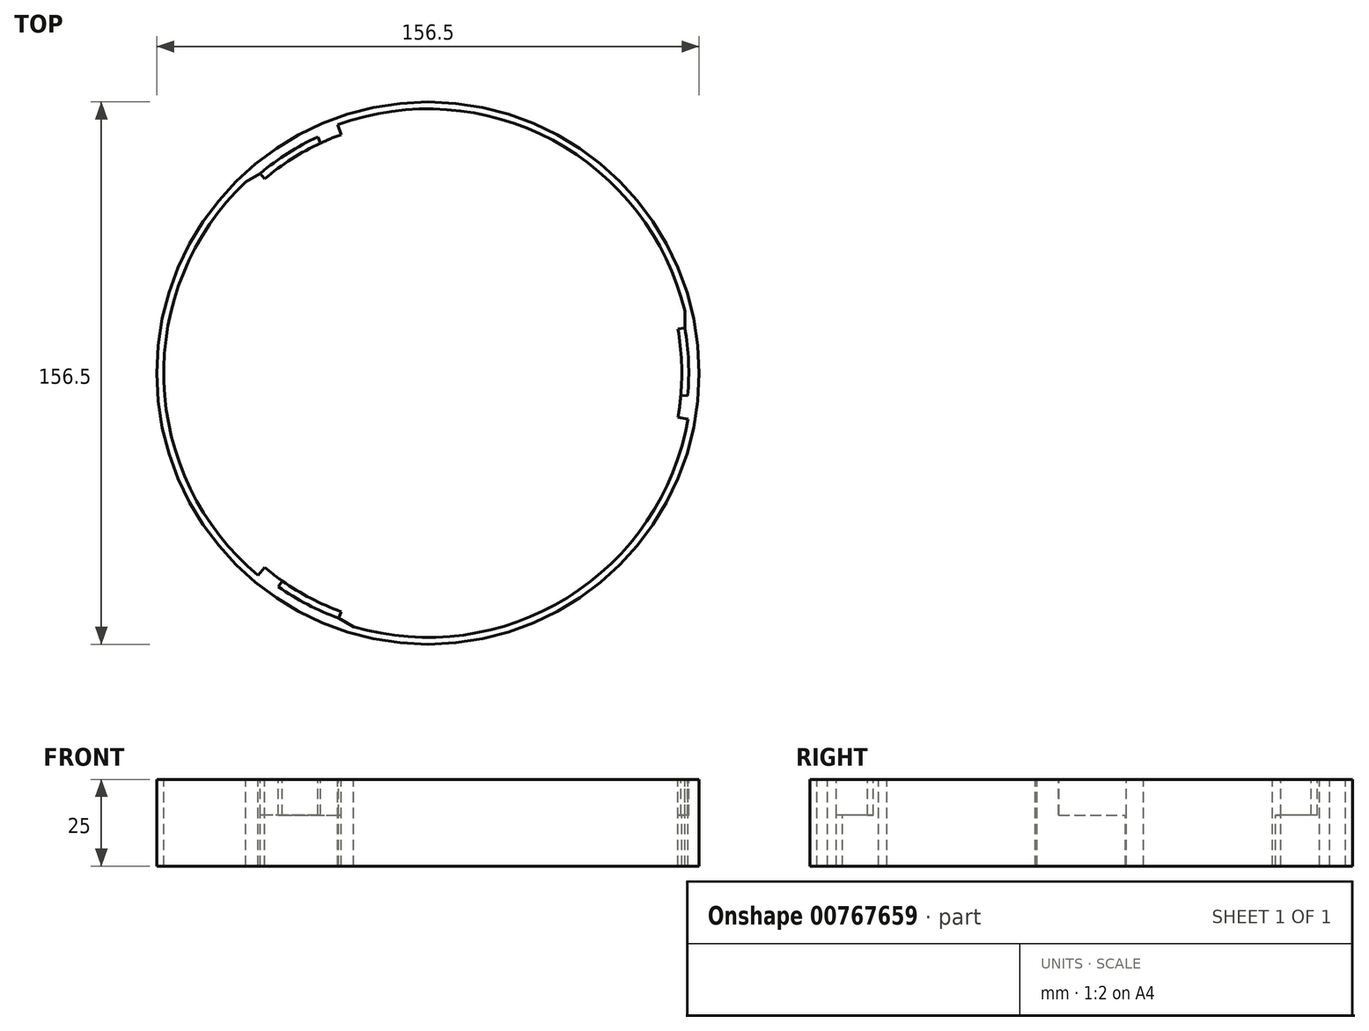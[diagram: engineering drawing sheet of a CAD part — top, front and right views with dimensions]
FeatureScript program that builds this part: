
annotation { "Feature Type Name" : "Feature", "Feature Type Description" : "" }
export const myFeature = defineFeature(function(context is Context, id is Id, definition is map)
    precondition{}
    {
        {
            var Q0;
            Q0=qCreatedBy(makeId("Top.planeOp"),FACE);
            var sketch = newSketch(context, id + "F0", { "sketchPlane" : qUnion([Q0])});
            skArc(sketch, "E0", {"start": v(-31.8, 68.2) * mm, "mid": v(-40.43, 63.47) * mm, "end": v(-48.37, 57.64) * mm});
            skCircle(sketch, "E1", {"center": v(0, 0) * mm, "radius": 78.25 * mm});
            skArc(sketch, "E2", {"start": v(-25.05, 68.83) * mm, "mid": v(-36.63, 63.44) * mm, "end": v(-47.08, 56.11) * mm});
            skLineSegment(sketch, "E3", {"start": v(-47.08, 56.11) * mm, "end": v(-48.37, 57.64) * mm});
            skLineSegment(sketch, "E4", {"start": v(-48.37, 57.64) * mm, "end": v(-52.6, 55.2) * mm});
            skArc(sketch, "E5.trimOffspring", {"start": v(-52.6, 55.2) * mm, "mid": v(-76.21, -2.4) * mm, "end": v(-49.01, -58.41) * mm});
            skLineSegment(sketch, "E6", {"start": v(-25.05, 68.83) * mm, "end": v(-26.08, 71.65) * mm});
            skLineSegment(sketch, "E7", {"start": v(-31.8, 68.2) * mm, "end": v(-30.96, 66.39) * mm});
            skLineSegment(sketch, "E8.1.0", {"start": v(74.1, 13.07) * mm, "end": v(74.1, 17.95) * mm});
            skArc(sketch, "E8.1.1", {"start": v(74.96, -6.56) * mm, "mid": v(75.18, 3.28) * mm, "end": v(74.1, 13.07) * mm});
            skLineSegment(sketch, "E8.1.2", {"start": v(72.14, 12.72) * mm, "end": v(74.1, 13.07) * mm});
            skArc(sketch, "E8.1.3", {"start": v(72.14, -12.72) * mm, "mid": v(73.25, 0) * mm, "end": v(72.14, 12.72) * mm});
            skLineSegment(sketch, "E8.1.4", {"start": v(74.96, -6.56) * mm, "end": v(72.97, -6.38) * mm});
            skLineSegment(sketch, "E8.1.5", {"start": v(72.14, -12.72) * mm, "end": v(75.1, -13.24) * mm});
            skLineSegment(sketch, "E8.2.0", {"start": v(-25.74, -70.71) * mm, "end": v(-21.5, -73.15) * mm});
            skArc(sketch, "E8.2.1", {"start": v(-43.16, -61.64) * mm, "mid": v(-34.75, -66.75) * mm, "end": v(-25.74, -70.71) * mm});
            skLineSegment(sketch, "E8.2.2", {"start": v(-25.05, -68.83) * mm, "end": v(-25.74, -70.71) * mm});
            skArc(sketch, "E8.2.3", {"start": v(-47.08, -56.11) * mm, "mid": v(-36.62, -63.44) * mm, "end": v(-25.05, -68.83) * mm});
            skLineSegment(sketch, "E8.2.4", {"start": v(-43.16, -61.64) * mm, "end": v(-42.01, -60) * mm});
            skLineSegment(sketch, "E8.2.5", {"start": v(-47.08, -56.11) * mm, "end": v(-49.01, -58.41) * mm});
            skLineSegment(sketch, "E8.anchor1", {"start": v(0, 0) * mm, "end": v(-52.6, 55.2) * mm, "construction": true});
            skLineSegment(sketch, "E8.anchor2", {"start": v(0, 0) * mm, "end": v(-21.5, -73.15) * mm, "construction": true});
            skArc(sketch, "E9.trimOffspring", {"start": v(74.1, 17.95) * mm, "mid": v(36.02, 67.2) * mm, "end": v(-26.08, 71.65) * mm});
            skArc(sketch, "E10.trimOffspring", {"start": v(-21.5, -73.15) * mm, "mid": v(40.19, -64.8) * mm, "end": v(75.1, -13.24) * mm});
            skSolve(sketch);
        }
        {
            var Q0;
            Q0=makeQuery(id+"F0.imprint","IMPRINT",FACE,{"disambiguationData":[TD([[makeQuery(id+"F0.imprint","IMPRINT",EDGE,{"derivedFrom":sQuery(id+"F0.wireOp",EDGE,"E0")}),-1.0]])]});
            var Q1;
            Q1=makeQuery(id+"F0.imprint","IMPRINT",FACE,{"disambiguationData":[TD([[makeQuery(id+"F0.imprint","IMPRINT",EDGE,{"derivedFrom":sQuery(id+"F0.wireOp",EDGE,"E8.1.1")}),1.0]])]});
            var Q2;
            Q2=makeQuery(id+"F0.imprint","IMPRINT",FACE,{"disambiguationData":[TD([[makeQuery(id+"F0.imprint","IMPRINT",EDGE,{"derivedFrom":sQuery(id+"F0.wireOp",EDGE,"E8.2.1")}),1.0]])]});
            var Q3;
            Q3=makeQuery(id+"F0.imprint","IMPRINT",FACE,{"disambiguationData":[TD([[makeQuery(id+"F0.imprint","IMPRINT",EDGE,{"derivedFrom":sQuery(id+"F0.wireOp",EDGE,"E0")}),1.0]])]});
            extrude(context, id + "F1", {"entities" : qUnion([Q0, Q1, Q2, Q3]), "oppositeDirection" : true, "depth" : 25 * mm, "offsetDistance" : 25 * mm});
        }
        {
            var Q0;
            Q0=makeQuery(id+"F0.imprint","IMPRINT",FACE,{"disambiguationData":[TD([[makeQuery(id+"F0.imprint","IMPRINT",EDGE,{"derivedFrom":sQuery(id+"F0.wireOp",EDGE,"E8.1.1")}),1.0]])]});
            var Q1;
            Q1=makeQuery(id+"F0.imprint","IMPRINT",FACE,{"disambiguationData":[TD([[makeQuery(id+"F0.imprint","IMPRINT",EDGE,{"derivedFrom":sQuery(id+"F0.wireOp",EDGE,"E0")}),1.0]])]});
            var Q2;
            Q2=makeQuery(id+"F0.imprint","IMPRINT",FACE,{"disambiguationData":[TD([[makeQuery(id+"F0.imprint","IMPRINT",EDGE,{"derivedFrom":sQuery(id+"F0.wireOp",EDGE,"E8.2.1")}),1.0]])]});
            extrude(context, id + "F2", {"entities" : qUnion([Q0, Q1, Q2]), "operationType" : NewBodyOperationType.REMOVE, "oppositeDirection" : true, "depth" : 10.25 * mm, "offsetDistance" : 25 * mm});
        }
    });
